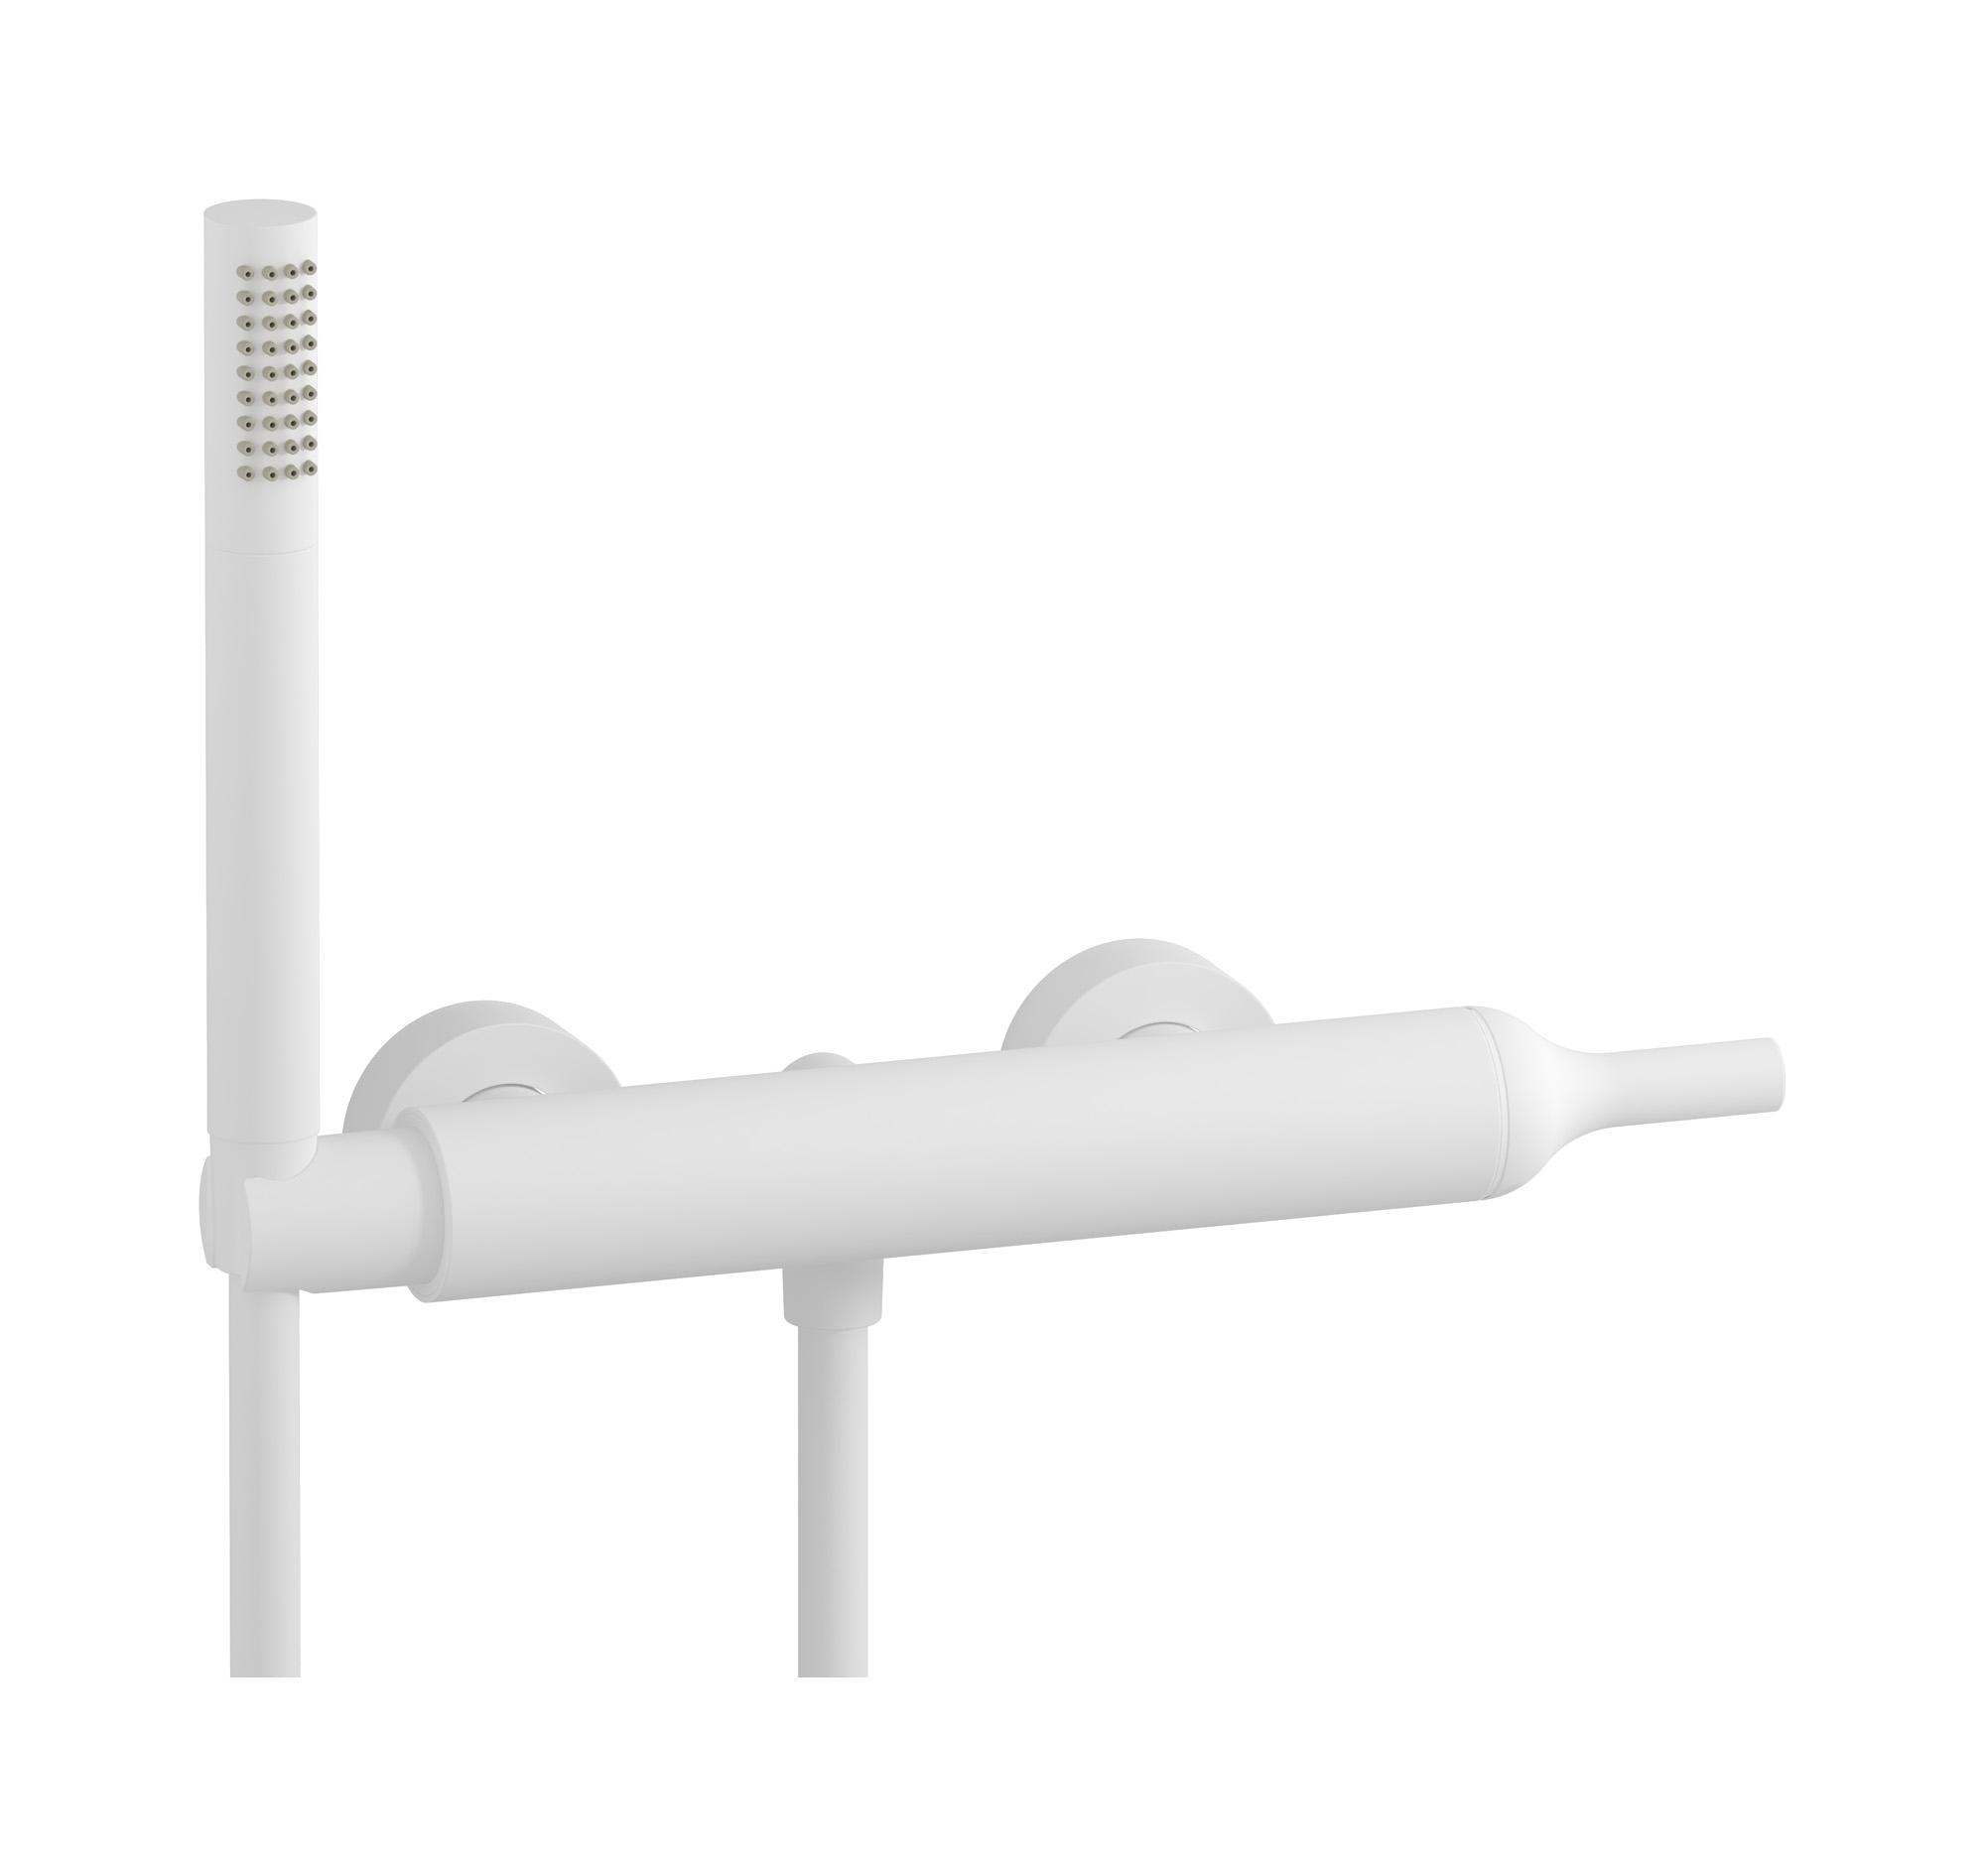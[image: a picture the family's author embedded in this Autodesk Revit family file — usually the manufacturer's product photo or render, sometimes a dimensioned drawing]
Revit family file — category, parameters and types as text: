
# Revit family: BI350
name_source: partatom
category: Apparecchi idraulici
units: mm (PartAtom-declared; Revit-internal decimal feet)

## family parameters
Basato su piano di lavoro = No
Condiviso = No
Mantieni orientamento annotazione = No
Numero OmniClass = 23.45.55.17
Punto di calcolo locali = No
Quota connettore circolare = Usa diametro
Sempre verticale = Sì
Taglio con vuoti quando caricato = No
Tipo di parte = Normale
Titolo OmniClass = Mixing Faucets

## types (4) — shared parameters
Cold water inlet = 10 mm  [stored 0.0328084 ft]
Commenti sul tipo = Shower mixer
Connessione CW = No
Connessione HW = No
Connessione di scarico = No
Connessione di ventilazione = No
Descrizione = Wall mounted shower mixer with shower kit
Hot water inlet = 10 mm  [stored 0.0328084 ft]
Produttore = IB Rubinetterie S.p.A.
URL = https://www.weareib.it
zero-valued in all types: Prospetto di default

## per-type parameters (varying)
| type | Finishes surface | Immagine tipo | Modello |
| Chrome | IB_Chrome | BI350CC.jpg | BI350CC |
| Brushed nickel | IB_Brushed nickel | BI350SS.jpg | BI350SS |
| Matt white | IB_matt white | BI350BO.jpg | BI350BO |
| Matt black | IB_matt black | BI350NP.jpg | BI350NP |

note: [stored X ft] marks values corroborated as IEEE doubles in the binary element streams (Revit-internal decimal feet)
